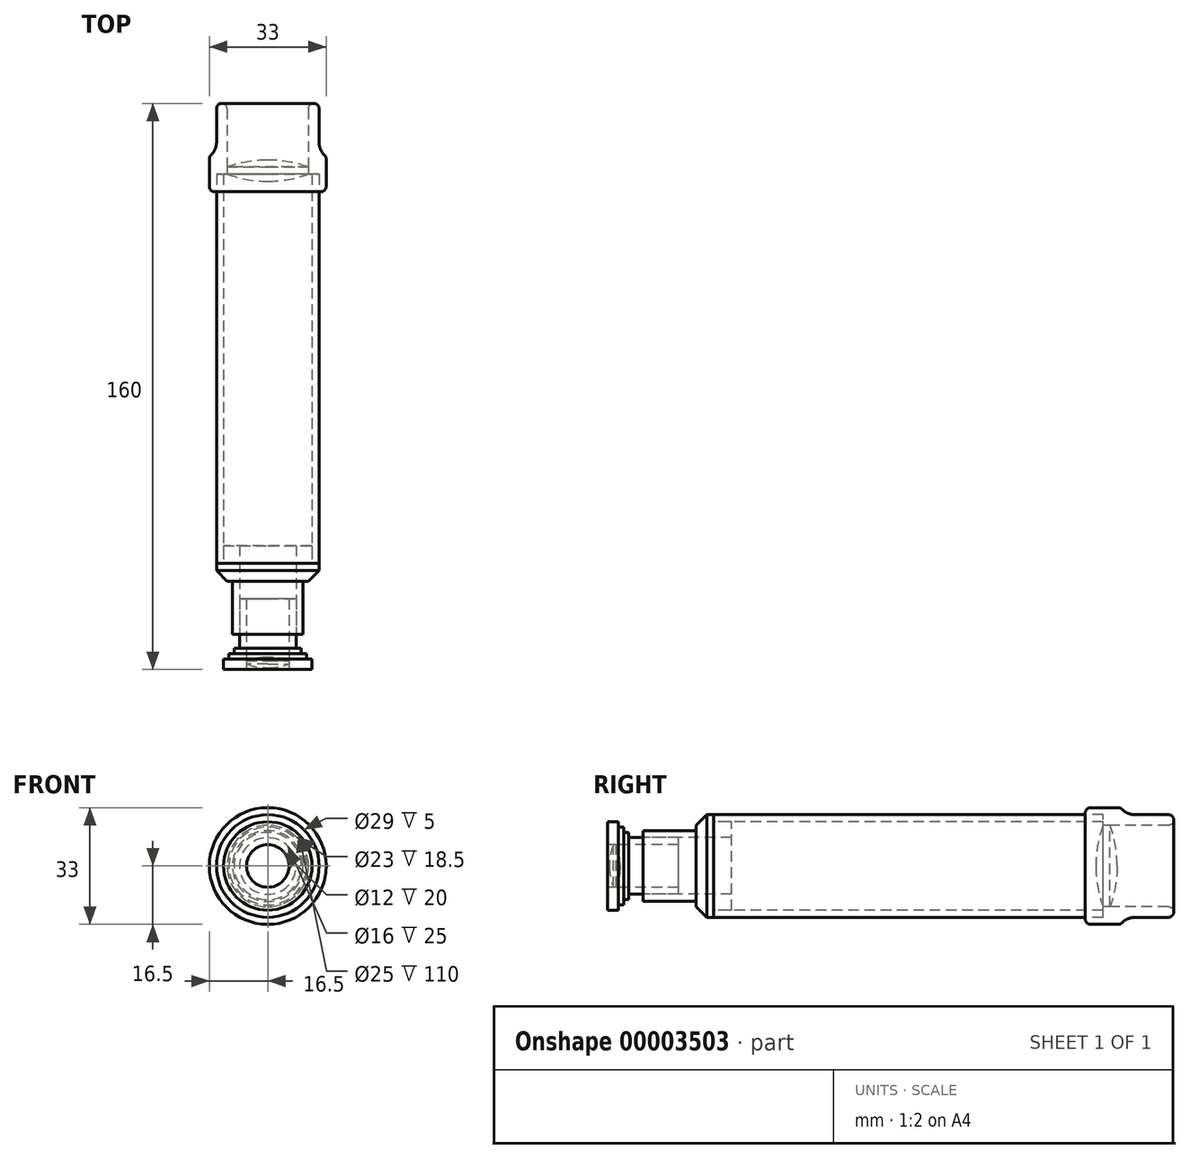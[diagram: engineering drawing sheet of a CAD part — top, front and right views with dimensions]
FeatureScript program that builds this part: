
annotation { "Feature Type Name" : "Feature", "Feature Type Description" : "" }
export const myFeature = defineFeature(function(context is Context, id is Id, definition is map)
    precondition{}
    {
        {
            var Q0;
            Q0=qCreatedBy(makeId("Right.planeOp"),FACE);
            var sketch = newSketch(context, id + "F0", { "sketchPlane" : qUnion([Q0])});
            skLineSegment(sketch, "E0", {"start": v(-80, 0) * mm, "end": v(80, 0) * mm, "construction": true});
            skLineSegment(sketch, "E1", {"start": v(-50, 14.5) * mm, "end": v(60, 14.5) * mm, "construction": true});
            skLineSegment(sketch, "E2.bottom", {"start": v(-50, 14.5) * mm, "end": v(60, 14.5) * mm});
            skLineSegment(sketch, "E2.top", {"start": v(-50, 12.5) * mm, "end": v(60, 12.5) * mm});
            skLineSegment(sketch, "E2.left", {"start": v(-50, 14.5) * mm, "end": v(-50, 12.5) * mm});
            skLineSegment(sketch, "E2.right", {"start": v(60, 14.5) * mm, "end": v(60, 12.5) * mm});
            skLineSegment(sketch, "E3", {"start": v(55, 14.5) * mm, "end": v(55, 16.5) * mm});
            skLineSegment(sketch, "E4", {"start": v(55, 16.5) * mm, "end": v(65, 16.5) * mm});
            skLineSegment(sketch, "E5", {"start": v(65, 16.5) * mm, "end": v(65, 14.5) * mm});
            skLineSegment(sketch, "E6", {"start": v(65, 14.5) * mm, "end": v(80, 14.5) * mm});
            skLineSegment(sketch, "E7", {"start": v(80, 14.5) * mm, "end": v(80, 11.5) * mm});
            skLineSegment(sketch, "E8", {"start": v(80, 11.5) * mm, "end": v(60, 11.5) * mm});
            skLineSegment(sketch, "E9", {"start": v(60, 11.5) * mm, "end": v(60, 12.5) * mm});
            skLineSegment(sketch, "E10", {"start": v(-50, 14.5) * mm, "end": v(-55, 14.5) * mm});
            skLineSegment(sketch, "E11", {"start": v(-55, 14.5) * mm, "end": v(-55, 10) * mm});
            skLineSegment(sketch, "E12", {"start": v(-55, 10) * mm, "end": v(-70, 10) * mm});
            skLineSegment(sketch, "E13", {"start": v(-70, 10) * mm, "end": v(-70, 8) * mm});
            skLineSegment(sketch, "E14", {"start": v(-70, 8) * mm, "end": v(-45, 8) * mm});
            skLineSegment(sketch, "E15", {"start": v(-45, 8) * mm, "end": v(-45, 12.5) * mm});
            skArc(sketch, "E16", {"start": v(60, 11.5) * mm, "mid": v(58.5, 5.84) * mm, "end": v(58, 0) * mm});
            skArc(sketch, "E17", {"start": v(64, 0) * mm, "mid": v(63.5, 5.84) * mm, "end": v(62, 11.5) * mm});
            skLineSegment(sketch, "E18", {"start": v(58, 0) * mm, "end": v(64, 0) * mm});
            skLineSegment(sketch, "E19", {"start": v(-60, 8) * mm, "end": v(-60, 6) * mm});
            skLineSegment(sketch, "E20", {"start": v(-60, 6) * mm, "end": v(-80, 6) * mm});
            skLineSegment(sketch, "E21", {"start": v(-80, 6) * mm, "end": v(-80, 12.5) * mm});
            skLineSegment(sketch, "E22", {"start": v(-80, 12.5) * mm, "end": v(-77, 12.5) * mm});
            skLineSegment(sketch, "E23", {"start": v(-77, 12.5) * mm, "end": v(-77, 11) * mm});
            skLineSegment(sketch, "E24", {"start": v(-77, 11) * mm, "end": v(-75.5, 11) * mm});
            skLineSegment(sketch, "E25", {"start": v(-75.5, 11) * mm, "end": v(-75.5, 9.5) * mm});
            skLineSegment(sketch, "E26", {"start": v(-75.5, 9.5) * mm, "end": v(-74, 9.5) * mm});
            skLineSegment(sketch, "E27", {"start": v(-74, 9.5) * mm, "end": v(-74, 8) * mm});
            skLineSegment(sketch, "E28", {"start": v(-74, 8) * mm, "end": v(-70, 8) * mm});
            skArc(sketch, "E29", {"start": v(-78.43, 6) * mm, "mid": v(-79.23, 3.05) * mm, "end": v(-79.5, 0) * mm});
            skArc(sketch, "E30", {"start": v(-76.5, 0) * mm, "mid": v(-76.77, 3.05) * mm, "end": v(-77.57, 6) * mm});
            skLineSegment(sketch, "E31", {"start": v(-79.5, 0) * mm, "end": v(-76.5, 0) * mm});
            skPoint(sketch, "E32", {"position": v(-78, 0) * mm});
            skSolve(sketch);
        }
        {
            var Q0;
            {var subQ1=sQuery(id+"F0.wireOp",EDGE,"E2.left");Q0=makeQuery(id+"F0.imprint","IMPRINT",FACE,{"disambiguationData":[TD([[makeQuery(id+"F0.imprint","IMPRINT",EDGE,{"derivedFrom":subQ1}),1.0]])]});}
            var Q1;
            Q1=sQuery(id+"F0.wireOp",EDGE,"E0");
            revolve(context, id + "F1", {"entities" : qUnion([Q0]), "axis" : qUnion([Q1]), "revolveType" : RevolveType.FULL});
        }
        {
            var Q0;
            {var subQ5=sQuery(id+"F0.wireOp",EDGE,"E19");Q0=makeQuery(id+"F0.imprint","IMPRINT",FACE,{"disambiguationData":[TD([[makeQuery(id+"F0.imprint","IMPRINT",EDGE,{"derivedFrom":subQ5}),-1.0]])]});}
            var Q1;
            Q1=sQuery(id+"F0.wireOp",EDGE,"E0");
            revolve(context, id + "F2", {"entities" : qUnion([Q0]), "axis" : qUnion([Q1]), "revolveType" : RevolveType.FULL});
        }
        {
            var Q0;
            {var subQ4=sQuery(id+"F0.wireOp",EDGE,"E2.left");Q0=makeQuery(id+"F0.imprint","IMPRINT",FACE,{"disambiguationData":[TD([[makeQuery(id+"F0.imprint","IMPRINT",EDGE,{"derivedFrom":subQ4}),-1.0]])]});}
            var Q1;
            Q1=sQuery(id+"F0.wireOp",EDGE,"E0");
            revolve(context, id + "F3", {"entities" : qUnion([Q0]), "axis" : qUnion([Q1]), "revolveType" : RevolveType.FULL});
        }
        {
            var Q0;
            {var subQ5=sQuery(id+"F0.wireOp",EDGE,"E2.right");Q0=makeQuery(id+"F0.imprint","IMPRINT",FACE,{"disambiguationData":[TD([[makeQuery(id+"F0.imprint","IMPRINT",EDGE,{"derivedFrom":subQ5}),1.0]])]});}
            var Q1;
            Q1=sQuery(id+"F0.wireOp",EDGE,"E0");
            revolve(context, id + "F4", {"entities" : qUnion([Q0]), "axis" : qUnion([Q1]), "revolveType" : RevolveType.FULL});
        }
        {
            var Q0;
            {var subQ1=sQuery(id+"F0.wireOp",EDGE,"E16");Q0=makeQuery(id+"F0.imprint","IMPRINT",FACE,{"disambiguationData":[TD([[makeQuery(id+"F0.imprint","IMPRINT",EDGE,{"derivedFrom":subQ1}),1.0]])]});}
            var Q1;
            Q1=sQuery(id+"F0.wireOp",EDGE,"E0");
            revolve(context, id + "F5", {"entities" : qUnion([Q0]), "axis" : qUnion([Q1]), "revolveType" : RevolveType.FULL});
        }
        {
            var Q0;
            {var subQ1=sQuery(id+"F0.wireOp",EDGE,"E29");Q0=makeQuery(id+"F0.imprint","IMPRINT",FACE,{"disambiguationData":[TD([[makeQuery(id+"F0.imprint","IMPRINT",EDGE,{"derivedFrom":subQ1}),1.0]])]});}
            var Q1;
            Q1=sQuery(id+"F0.wireOp",EDGE,"E0");
            revolve(context, id + "F6", {"entities" : qUnion([Q0]), "axis" : qUnion([Q1]), "revolveType" : RevolveType.FULL});
        }
        {
            var Q0;
            Q0=makeQuery(id+"F3.opRevolve","SWEPT_EDGE",EDGE,{"disambiguationData":[OSD([sQuery(id+"F0.wireOp",EDGE,"E10"),sQuery(id+"F0.wireOp",EDGE,"E11")])]});
            chamfer(context, id + "F7", {"entities" : qUnion([Q0]), "width" : 3 * mm, "tangentPropagation" : true});
        }
        {
            var Q0;
            Q0=makeQuery(id+"F4.opRevolve","SWEPT_EDGE",EDGE,{"disambiguationData":[OSD([sQuery(id+"F0.wireOp",EDGE,"E5"),sQuery(id+"F0.wireOp",EDGE,"E6")])]});
            fillet(context, id + "F8", {"entities" : qUnion([Q0]), "radius" : 5 * mm, "tangentPropagation" : true, "allowEdgeOverflow" : false});
        }
        {
            var Q0;
            Q0=makeQuery(id+"F4.opRevolve","SWEPT_EDGE",EDGE,{"disambiguationData":[OSD([sQuery(id+"F0.wireOp",EDGE,"E6"),sQuery(id+"F0.wireOp",EDGE,"E7")])]});
            var Q1;
            Q1=makeQuery(id+"F4.opRevolve","SWEPT_EDGE",EDGE,{"disambiguationData":[OSD([sQuery(id+"F0.wireOp",EDGE,"E7"),sQuery(id+"F0.wireOp",EDGE,"E8")])]});
            var Q2;
            Q2=makeQuery(id+"F4.opRevolve","SWEPT_FACE",FACE,{"disambiguationData":[OSD([sQuery(id+"F0.wireOp",EDGE,"E4")])]});
            fillet(context, id + "F9", {"entities" : qUnion([Q0, Q1, Q2]), "radius" : 1.5 * mm, "tangentPropagation" : true, "allowEdgeOverflow" : false});
        }
    });
